# Revit family: Plumbing_Drainage_Dallmer_Zentrix
name_source: partatom
category: Plumbing Fixtures
revit_build: Autodesk Revit 2015 (Build: 20140606_1530(x64)
units: mm (PartAtom-declared; Revit-internal decimal feet)

## types (1)
- Zentrix 300x50mm
    Assembly Code = D2030300
    BIMobject category = Drainage
    BIMobject category code = plumbing-drainage
    BIMobject main category = Plumbing
    BIMobject main category code = plumbing
    Brand url = http://www.dallmer.com
    Description = Shower Channel
    Design country = Germany
    Edition number = 1
    Installation instructions = http://www.dallmer.de
    Keynote = 15150.A2
    Manufacturer = Dallmer
    Manufacturer country = Germany
    Manufacturer name = Dallmer
    Material main = Stainless steel
    Material secondary = Polypropylene
    Model = Zentrix
    Nominal height = 0
    Nominal width = 0
    Product Guid = 14989c81-8dde-429e-b9d4-51a3c70b5522
    Product SKU = shower-channels-zentrix-511317511355
    Product data url = https://bimobject.com
    Product family = Shower channel
    Product group = DallFlex
    Product url = http://www.dallmer.de
    QR code = http://bimobject.com
    UNSPSC Code = 40141719
    URL = http://www.dallmer.com
    Uniclass 1.4 Code = JR1
    Uniclass 1.4 Description = Drainage
    Uniclass 2.0 Code = PR-62-24
    Uniclass 2.0 Description = Drainage Traps
    Uniclass 2015 Code = Ac_10_40_67
    Uniclass 2015 Name = Plumbing
    Uniformat II Code = D2010
    Uniformat II Description = Plumbing Fixtures
    Weight Net (Kg) = 0

## geometry (parser evidence)
native form markers: Blend x2, Sweep x13
no freeform markers — native parametric forms only
